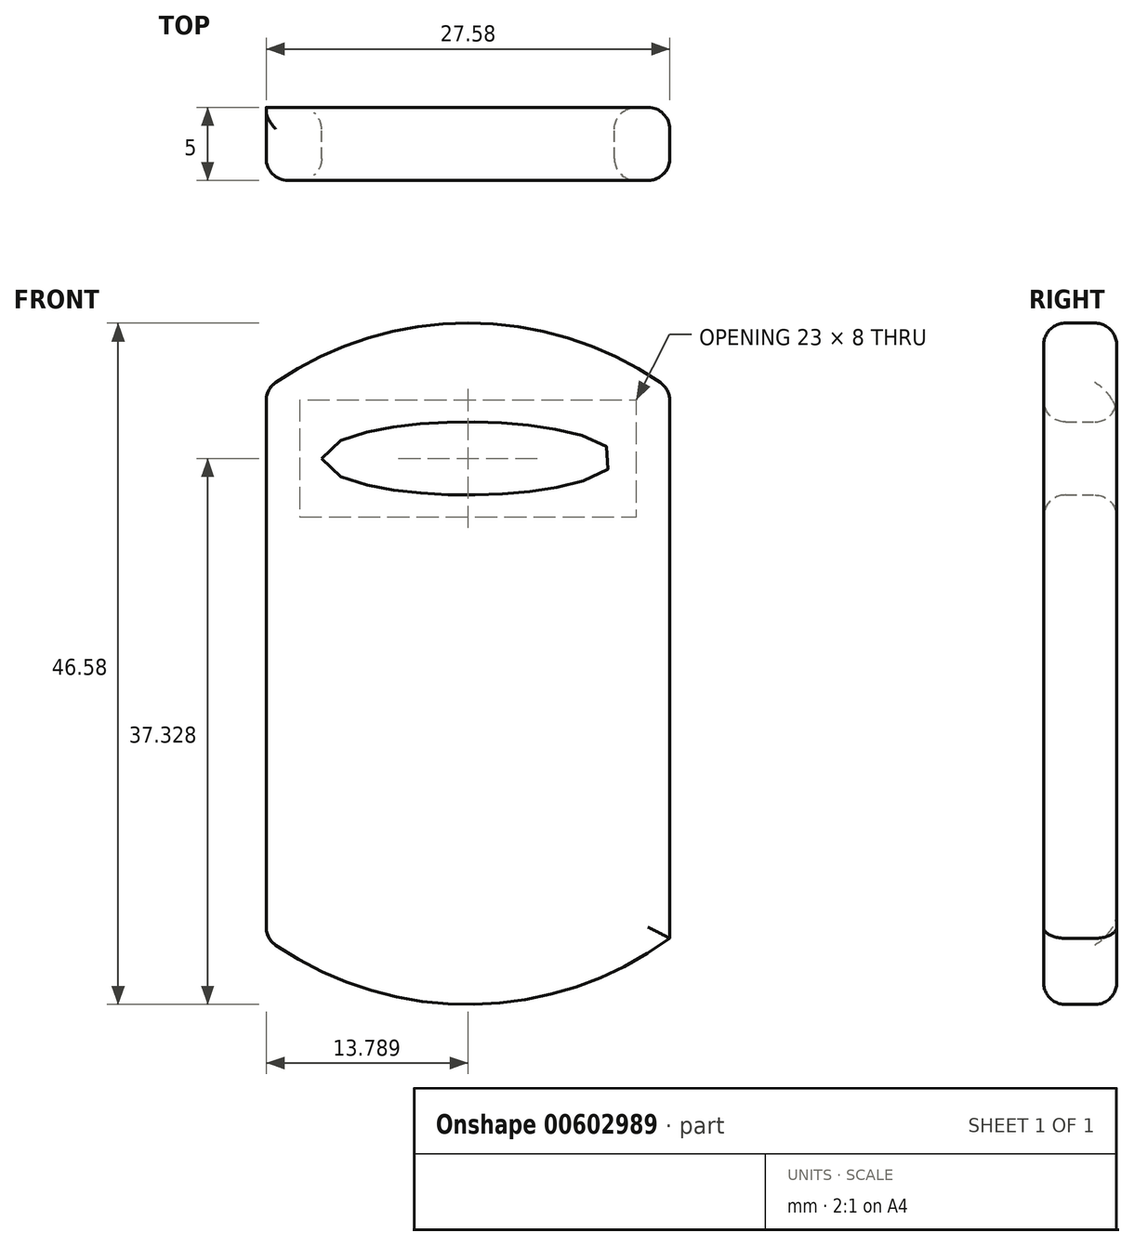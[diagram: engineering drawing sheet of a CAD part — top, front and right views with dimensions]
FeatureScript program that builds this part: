
annotation { "Feature Type Name" : "Feature", "Feature Type Description" : "" }
export const myFeature = defineFeature(function(context is Context, id is Id, definition is map)
    precondition{}
    {
        {
            var Q0;
            Q0=qCreatedBy(makeId("Front.planeOp"),FACE);
            var sketch = newSketch(context, id + "F0", { "sketchPlane" : qUnion([Q0])});
            skEllipse(sketch, "E0", {"center": v(0, 42.39) * mm, "majorRadius": 10 * mm, "minorRadius": 2.5 * mm, "majorAxis": v(-1, 0)});
            skArc(sketch, "E1", {"start": v(13.8, 47.12) * mm, "mid": v(0, 51.64) * mm, "end": v(-13.8, 47.12) * mm});
            skArc(sketch, "E2.MirrorCS", {"start": v(13.8, 9.58) * mm, "mid": v(0, 5.06) * mm, "end": v(-13.8, 9.58) * mm});
            skLineSegment(sketch, "E3", {"start": v(13.8, 47.12) * mm, "end": v(13.8, 9.58) * mm});
            skLineSegment(sketch, "E4", {"start": v(-13.8, 47.12) * mm, "end": v(-13.8, 9.58) * mm});
            skSolve(sketch);
        }
        {
            var Q0;
            Q0=makeQuery(id+"F0.imprint","IMPRINT",FACE,{"disambiguationData":[TD([[makeQuery(id+"F0.imprint","IMPRINT",EDGE,{"derivedFrom":sQuery(id+"F0.wireOp",EDGE,"E0")}),-1.0]])]});
            extrude(context, id + "F1", {"entities" : qUnion([Q0]), "depth" : 5 * mm, "offsetDistance" : 25 * mm});
        }
        {
            var Q0;
            Q0=makeQuery(id+"F1.opExtrude","CAP_EDGE",EDGE,{"disambiguationData":[OSD([sQuery(id+"F0.wireOp",EDGE,"E1")])],"isStart":false});
            var Q1;
            Q1=makeQuery(id+"F1.opExtrude","CAP_EDGE",EDGE,{"disambiguationData":[OSD([sQuery(id+"F0.wireOp",EDGE,"E4")])],"isStart":false});
            var Q2;
            Q2=makeQuery(id+"F1.opExtrude","CAP_EDGE",EDGE,{"disambiguationData":[OSD([sQuery(id+"F0.wireOp",EDGE,"E2.MirrorCS")])],"isStart":false});
            var Q3;
            Q3=makeQuery(id+"F1.opExtrude","CAP_EDGE",EDGE,{"disambiguationData":[OSD([sQuery(id+"F0.wireOp",EDGE,"E3")])],"isStart":false});
            var Q4;
            Q4=makeQuery(id+"F1.opExtrude","SWEPT_EDGE",EDGE,{"disambiguationData":[OSD([sQuery(id+"F0.wireOp",EDGE,"E1"),sQuery(id+"F0.wireOp",EDGE,"E4")])]});
            var Q5;
            Q5=makeQuery(id+"F1.opExtrude","SWEPT_EDGE",EDGE,{"disambiguationData":[OSD([sQuery(id+"F0.wireOp",EDGE,"E2.MirrorCS"),sQuery(id+"F0.wireOp",EDGE,"E4")])]});
            var Q6;
            Q6=makeQuery(id+"F1.opExtrude","CAP_EDGE",EDGE,{"disambiguationData":[OSD([sQuery(id+"F0.wireOp",EDGE,"E1")])],"isStart":true});
            var Q7;
            Q7=makeQuery(id+"F1.opExtrude","SWEPT_EDGE",EDGE,{"disambiguationData":[OSD([sQuery(id+"F0.wireOp",EDGE,"E1"),sQuery(id+"F0.wireOp",EDGE,"E3")])]});
            var Q8;
            Q8=makeQuery(id+"F1.opExtrude","CAP_EDGE",EDGE,{"disambiguationData":[OSD([sQuery(id+"F0.wireOp",EDGE,"E3")])],"isStart":true});
            var Q9;
            Q9=makeQuery(id+"F1.opExtrude","CAP_EDGE",EDGE,{"disambiguationData":[OSD([sQuery(id+"F0.wireOp",EDGE,"E2.MirrorCS")])],"isStart":true});
            var Q10;
            Q10=makeQuery(id+"F1.opExtrude","CAP_EDGE",EDGE,{"disambiguationData":[OSD([sQuery(id+"F0.wireOp",EDGE,"E0")])],"isStart":true});
            var Q11;
            Q11=makeQuery(id+"F1.opExtrude","CAP_EDGE",EDGE,{"disambiguationData":[OSD([sQuery(id+"F0.wireOp",EDGE,"E0")])],"isStart":false});
            fillet(context, id + "F2", {"entities" : qUnion([Q0, Q1, Q2, Q3, Q4, Q5, Q6, Q7, Q8, Q9, Q10, Q11]), "radius" : 1.5 * mm, "tangentPropagation" : true, "allowEdgeOverflow" : false});
        }
    });
